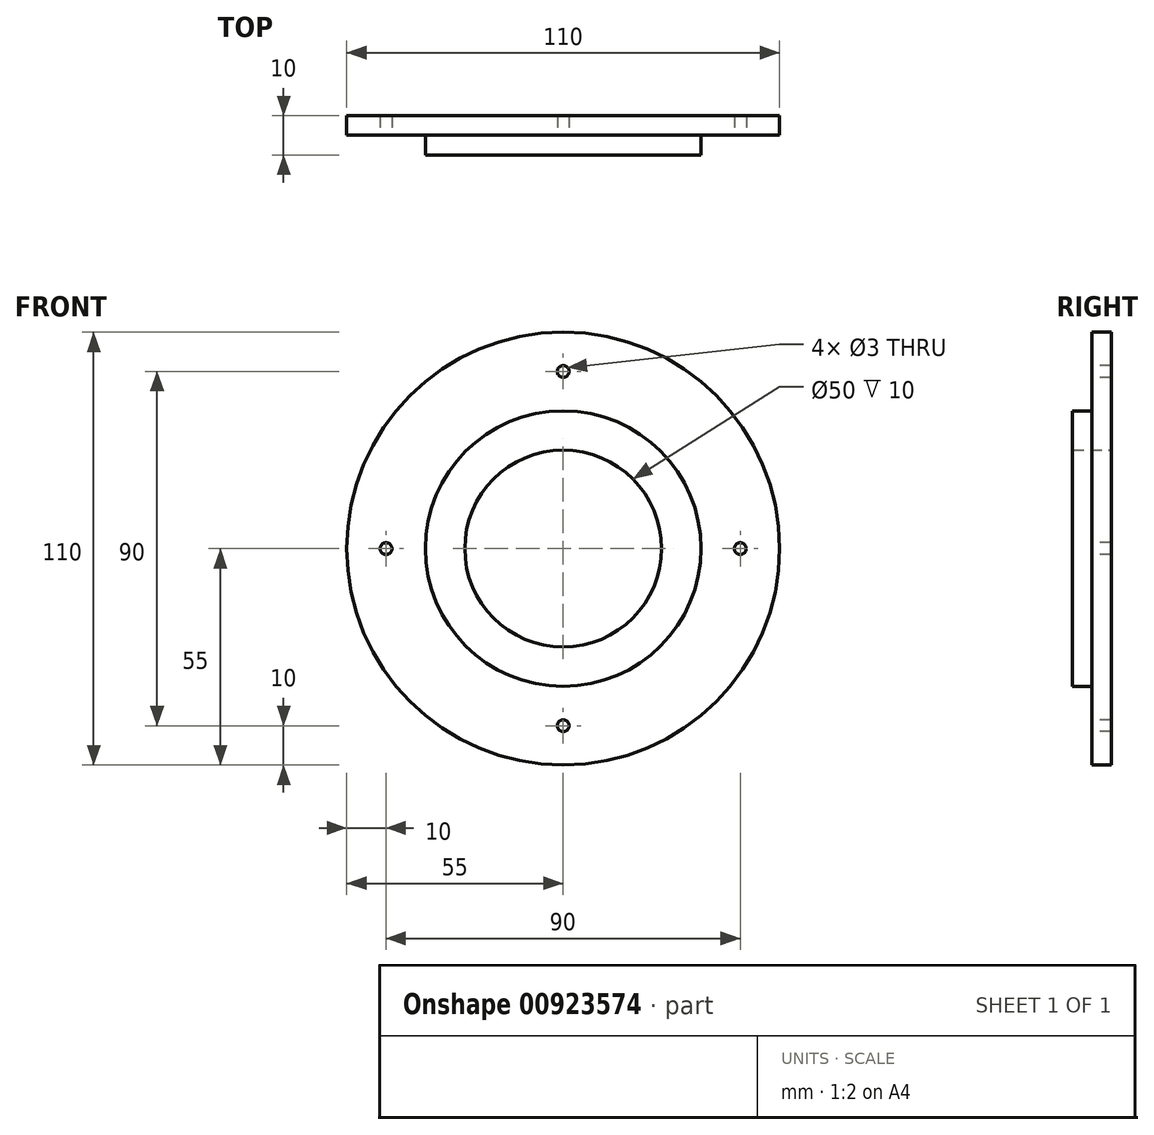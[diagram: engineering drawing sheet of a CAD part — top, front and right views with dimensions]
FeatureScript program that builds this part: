
annotation { "Feature Type Name" : "Feature", "Feature Type Description" : "" }
export const myFeature = defineFeature(function(context is Context, id is Id, definition is map)
    precondition{}
    {
        {
            var Q0;
            Q0=qCreatedBy(makeId("Front.planeOp"),FACE);
            var sketch = newSketch(context, id + "F0", { "sketchPlane" : qUnion([Q0])});
            skCircle(sketch, "E0", {"center": v(0, 0) * mm, "radius": 55 * mm});
            skSolve(sketch);
        }
        {
            var Q0;
            Q0=makeQuery(id+"F0.imprint","IMPRINT",FACE,{"disambiguationData":[TD([[makeQuery(id+"F0.imprint","IMPRINT",EDGE,{"derivedFrom":sQuery(id+"F0.wireOp",EDGE,"E0")}),1.0]])]});
            extrude(context, id + "F1", {"entities" : qUnion([Q0]), "depth" : 5 * mm, "offsetDistance" : 25 * mm});
        }
        {
            var Q0;
            Q0=makeQuery(id+"F1.opExtrude","CAP_FACE",FACE,{"disambiguationData":[OSD([sQuery(id+"F0.wireOp",EDGE,"E0")])],"isStart":false});
            var sketch = newSketch(context, id + "F2", { "sketchPlane" : qUnion([Q0])});
            skCircle(sketch, "E1", {"center": v(0, 0) * mm, "radius": 35 * mm});
            skSolve(sketch);
        }
        {
            var Q0;
            Q0=makeQuery(id+"F2.imprint","IMPRINT",FACE,{"disambiguationData":[TD([[makeQuery(id+"F2.imprint","IMPRINT",EDGE,{"derivedFrom":sQuery(id+"F2.wireOp",EDGE,"E1")}),1.0]])]});
            extrude(context, id + "F3", {"entities" : qUnion([Q0]), "operationType" : NewBodyOperationType.ADD, "depth" : 5 * mm, "offsetDistance" : 25 * mm});
        }
        {
            var Q0;
            Q0=makeQuery(id+"F1.opExtrude","CAP_FACE",FACE,{"disambiguationData":[OSD([sQuery(id+"F0.wireOp",EDGE,"E0")])],"isStart":true});
            var sketch = newSketch(context, id + "F4", { "sketchPlane" : qUnion([Q0])});
            skCircle(sketch, "E2", {"center": v(0, 0) * mm, "radius": 25 * mm});
            skSolve(sketch);
        }
        {
            var Q0;
            Q0=makeQuery(id+"F4.imprint","IMPRINT",FACE,{"disambiguationData":[TD([[makeQuery(id+"F4.imprint","IMPRINT",EDGE,{"derivedFrom":sQuery(id+"F4.wireOp",EDGE,"E2")}),1.0]])]});
            extrude(context, id + "F5", {"entities" : qUnion([Q0]), "operationType" : NewBodyOperationType.REMOVE, "oppositeDirection" : true, "depth" : 25 * mm, "offsetDistance" : 25 * mm});
        }
        {
            var Q0;
            Q0=makeQuery(id+"F3.opExtrude","CAP_FACE",FACE,{"disambiguationData":[OSD([sQuery(id+"F2.wireOp",EDGE,"E1")])],"isStart":false});
            var sketch = newSketch(context, id + "F6", { "sketchPlane" : qUnion([Q0])});
            skCircle(sketch, "E3", {"center": v(0, 0) * mm, "radius": 45 * mm, "construction": true});
            skCircle(sketch, "E4", {"center": v(-45, 0) * mm, "radius": 1.5 * mm});
            skCircle(sketch, "E5", {"center": v(0, 45) * mm, "radius": 1.5 * mm});
            skCircle(sketch, "E6", {"center": v(0, -45) * mm, "radius": 1.5 * mm});
            skCircle(sketch, "E7", {"center": v(45, 0) * mm, "radius": 1.5 * mm});
            skSolve(sketch);
        }
        {
            var Q0;
            Q0 = qSketchRegion(id + "F6", true);
            extrude(context, id + "F7", {"entities" : qUnion([Q0]), "operationType" : NewBodyOperationType.REMOVE, "oppositeDirection" : true, "depth" : 12 * mm, "offsetDistance" : 25 * mm});
        }
    });
